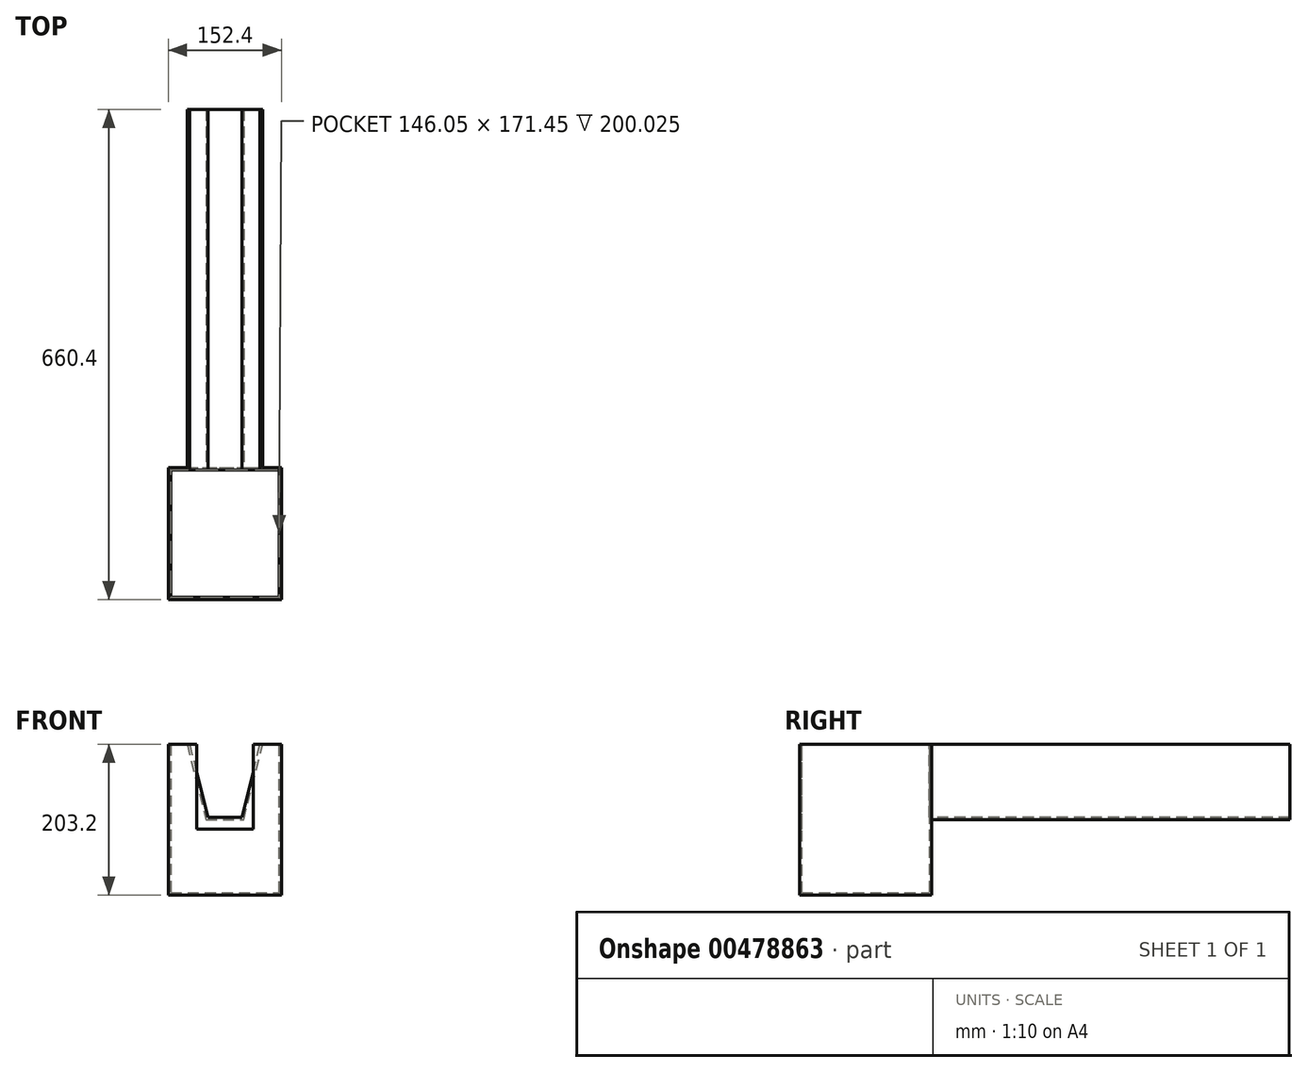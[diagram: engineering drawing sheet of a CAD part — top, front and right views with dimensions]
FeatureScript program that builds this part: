
annotation { "Feature Type Name" : "Feature", "Feature Type Description" : "" }
export const myFeature = defineFeature(function(context is Context, id is Id, definition is map)
    precondition{}
    {
        {
            var Q0;
            Q0=qCreatedBy(makeId("Front.planeOp"),FACE);
            var sketch = newSketch(context, id + "F0", { "sketchPlane" : qUnion([Q0])});
            skLineSegment(sketch, "E0", {"start": v(0, 0) * mm, "end": v(25.4, 0) * mm});
            skLineSegment(sketch, "E1", {"start": v(25.4, 0) * mm, "end": v(50.8, 101.6) * mm});
            skLineSegment(sketch, "E2", {"start": v(50.8, 101.6) * mm, "end": v(-50.8, 101.6) * mm});
            skLineSegment(sketch, "E3", {"start": v(-50.8, 101.6) * mm, "end": v(-25.4, 0) * mm});
            skLineSegment(sketch, "E4", {"start": v(-25.4, 0) * mm, "end": v(0, 0) * mm});
            skSolve(sketch);
        }
        {
            var Q0;
            Q0 = qSketchRegion(id + "F0", true);
            extrude(context, id + "F1", {"entities" : qUnion([Q0]), "oppositeDirection" : true, "depth" : 508 * mm});
        }
        {
            var Q0;
            Q0=qCreatedBy(makeId("Front.planeOp"),FACE);
            var sketch = newSketch(context, id + "F2", { "sketchPlane" : qUnion([Q0])});
            skLineSegment(sketch, "E5", {"start": v(76.2, 0) * mm, "end": v(76.2, 101.6) * mm});
            skLineSegment(sketch, "E6", {"start": v(76.2, 101.6) * mm, "end": v(-76.2, 101.6) * mm});
            skLineSegment(sketch, "E7", {"start": v(-76.2, 101.6) * mm, "end": v(-76.2, 0) * mm});
            skLineSegment(sketch, "E8", {"start": v(-76.2, 0) * mm, "end": v(-76.2, -101.6) * mm});
            skLineSegment(sketch, "E9", {"start": v(-76.2, -101.6) * mm, "end": v(76.2, -101.6) * mm});
            skLineSegment(sketch, "E10", {"start": v(76.2, -101.6) * mm, "end": v(76.2, 0) * mm});
            skSolve(sketch);
        }
        {
            var Q0;
            Q0 = qSketchRegion(id + "F2", true);
            extrude(context, id + "F3", {"entities" : qUnion([Q0]), "operationType" : NewBodyOperationType.ADD, "depth" : 177.8 * mm});
        }
        {
            var Q0;
            Q0=makeQuery(id+"F3.boolean.opBoolean","MERGE",FACE,{"derivedFrom":[makeQuery(id+"F1.opExtrude","SWEPT_FACE",FACE,{"disambiguationData":[OSD([sQuery(id+"F0.wireOp",EDGE,"E2")])]}),makeQuery(id+"F3.opExtrude","SWEPT_FACE",FACE,{"disambiguationData":[OSD([sQuery(id+"F2.wireOp",EDGE,"E6")])]})]});
            shell(context, id + "F4", {"entities" : qUnion([Q0]), "thickness" : 3.17 * mm});
        }
        {
            var Q0;
            Q0=makeQuery(id+"F1.opExtrude","CAP_FACE",FACE,{"disambiguationData":[OSD([sQuery(id+"F0.wireOp",EDGE,"E0"),sQuery(id+"F0.wireOp",EDGE,"E1"),sQuery(id+"F0.wireOp",EDGE,"E2"),sQuery(id+"F0.wireOp",EDGE,"E3"),sQuery(id+"F0.wireOp",EDGE,"E4")])],"isStart":false});
            var sketch = newSketch(context, id + "F5", { "sketchPlane" : qUnion([Q0])});
            skLineSegment(sketch, "E11", {"start": v(-50.8, 101.6) * mm, "end": v(50.8, 101.6) * mm});
            skLineSegment(sketch, "E12", {"start": v(50.8, 101.6) * mm, "end": v(25.4, 0) * mm});
            skLineSegment(sketch, "E13", {"start": v(25.4, 0) * mm, "end": v(-25.4, 0) * mm});
            skLineSegment(sketch, "E14", {"start": v(-25.4, 0) * mm, "end": v(-50.8, 101.6) * mm});
            skLineSegment(sketch, "E15.0", {"start": v(-22.92, 3.17) * mm, "end": v(-46.73, 98.43) * mm});
            skLineSegment(sketch, "E16.0", {"start": v(-50.8, 98.43) * mm, "end": v(-50, 98.43) * mm});
            skLineSegment(sketch, "E17.0", {"start": v(47.72, 102.37) * mm, "end": v(47.53, 101.6) * mm});
            skLineSegment(sketch, "E18.0", {"start": v(22.92, 3.17) * mm, "end": v(-22.92, 3.17) * mm});
            skLineSegment(sketch, "E19.trimOffspring", {"start": v(-47.53, 101.6) * mm, "end": v(-47.72, 102.37) * mm});
            skLineSegment(sketch, "E20.trimOffspring", {"start": v(46.73, 98.42) * mm, "end": v(22.92, 3.17) * mm});
            skLineSegment(sketch, "E21.trimOffspring", {"start": v(50, 98.42) * mm, "end": v(50.8, 98.42) * mm});
            skLineSegment(sketch, "E22", {"start": v(46.73, 98.42) * mm, "end": v(47.53, 101.6) * mm});
            skLineSegment(sketch, "E23", {"start": v(-47.53, 101.6) * mm, "end": v(-46.73, 98.43) * mm});
            skSolve(sketch);
        }
        {
            var Q0;
            Q0 = qSketchRegion(id + "F5", true);
            extrude(context, id + "F6", {"entities" : qUnion([Q0]), "operationType" : NewBodyOperationType.REMOVE, "oppositeDirection" : true, "depth" : 25.4 * mm});
        }
        {
            var Q0;
            Q0=makeQuery(id+"F3.opExtrude","CAP_FACE",FACE,{"disambiguationData":[OSD([sQuery(id+"F2.wireOp",EDGE,"E5"),sQuery(id+"F2.wireOp",EDGE,"E6"),sQuery(id+"F2.wireOp",EDGE,"E7"),sQuery(id+"F2.wireOp",EDGE,"E8"),sQuery(id+"F2.wireOp",EDGE,"E9"),sQuery(id+"F2.wireOp",EDGE,"E10")])],"isStart":false});
            var sketch = newSketch(context, id + "F7", { "sketchPlane" : qUnion([Q0])});
            skLineSegment(sketch, "E24", {"start": v(0, 0) * mm, "end": v(0, -12.7) * mm});
            skLineSegment(sketch, "E25", {"start": v(0, -12.7) * mm, "end": v(38.1, -12.7) * mm});
            skLineSegment(sketch, "E26", {"start": v(38.1, -12.7) * mm, "end": v(38.1, 101.6) * mm});
            skLineSegment(sketch, "E27", {"start": v(38.1, 101.6) * mm, "end": v(-38.1, 101.6) * mm});
            skLineSegment(sketch, "E28", {"start": v(-38.1, 101.6) * mm, "end": v(-38.1, -12.7) * mm});
            skLineSegment(sketch, "E29", {"start": v(-38.1, -12.7) * mm, "end": v(0, -12.7) * mm});
            skSolve(sketch);
        }
        {
            var Q0;
            Q0 = qSketchRegion(id + "F7", true);
            extrude(context, id + "F8", {"entities" : qUnion([Q0]), "operationType" : NewBodyOperationType.REMOVE, "oppositeDirection" : true, "depth" : 25.4 * mm});
        }
    });
